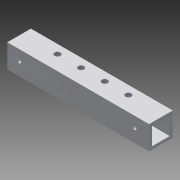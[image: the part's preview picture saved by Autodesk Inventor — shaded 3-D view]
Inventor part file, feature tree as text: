
AUTODESK INVENTOR PART (.ipt)
format: ipt  version: 2015 SP1 (Build 190203100, 203)  size: 137,216 bytes
history: native  units: in
note: dims shown in document units (in); Inventor stores cm internally (conversion verified against a paired STEP export)
features: sketch x5, hole x4, extrude x1
ambient origin geometry x8: Origin, YZ Plane, XZ Plane, XY Plane, X Axis, Y Axis, Z Axis, Center Point
bodies: Solid1 (feature_tree)
feature tree (10):
  extrude  "Extrusion1"  Depth=1.0in
  hole  "Hole1"  [1 undecoded]
  hole  "Hole2"  [1 undecoded]
  hole  "Hole3"  [1 undecoded]
  hole  "Hole4"  [1 undecoded]
  sketch  "Sketch1"  dims[d0=1.0in d1=1.0in]
  sketch  "Sketch2"  dims[d2=0.75in d3=0.75in]
  sketch  "Sketch3"  dims[d4=0.125in d5=0.125in]
  sketch  "Sketch4"  dims[d6=6.0in d7=0.0in d8=1.5in]
  sketch  "Sketch5"  dims[d9=0.625in d10=0.625in d11=1.5in d12=0.25in d13=0.75in d14=0.375in d15=0.25in d16=0.5635in d17=1.0in d18=0.8108in d19=0.625in d20=0.5625in d21=0.5in d22=0.5625in d23=0.1719in d24=0.75in d25=0.375in d26=0.25in d27=0.5635in d28=1.0in d29=0.8108in d30=0.625in d32=0.25in d33=0.75in d34=0.375in d35=0.25in d36=0.5635in d37=1.0in d38=0.8108in d39=2.5in d40=0.375in d41=1.0in d42=0.25in d43=0.75in d44=0.375in d45=0.25in d46=0.5635in d47=1.0in d48=0.8108in]
note: 4 required parameter values undecoded (feature->parameter linkage not recoverable at this tier; creation-order binding heuristic only, values carry confidence <= 0.55)
